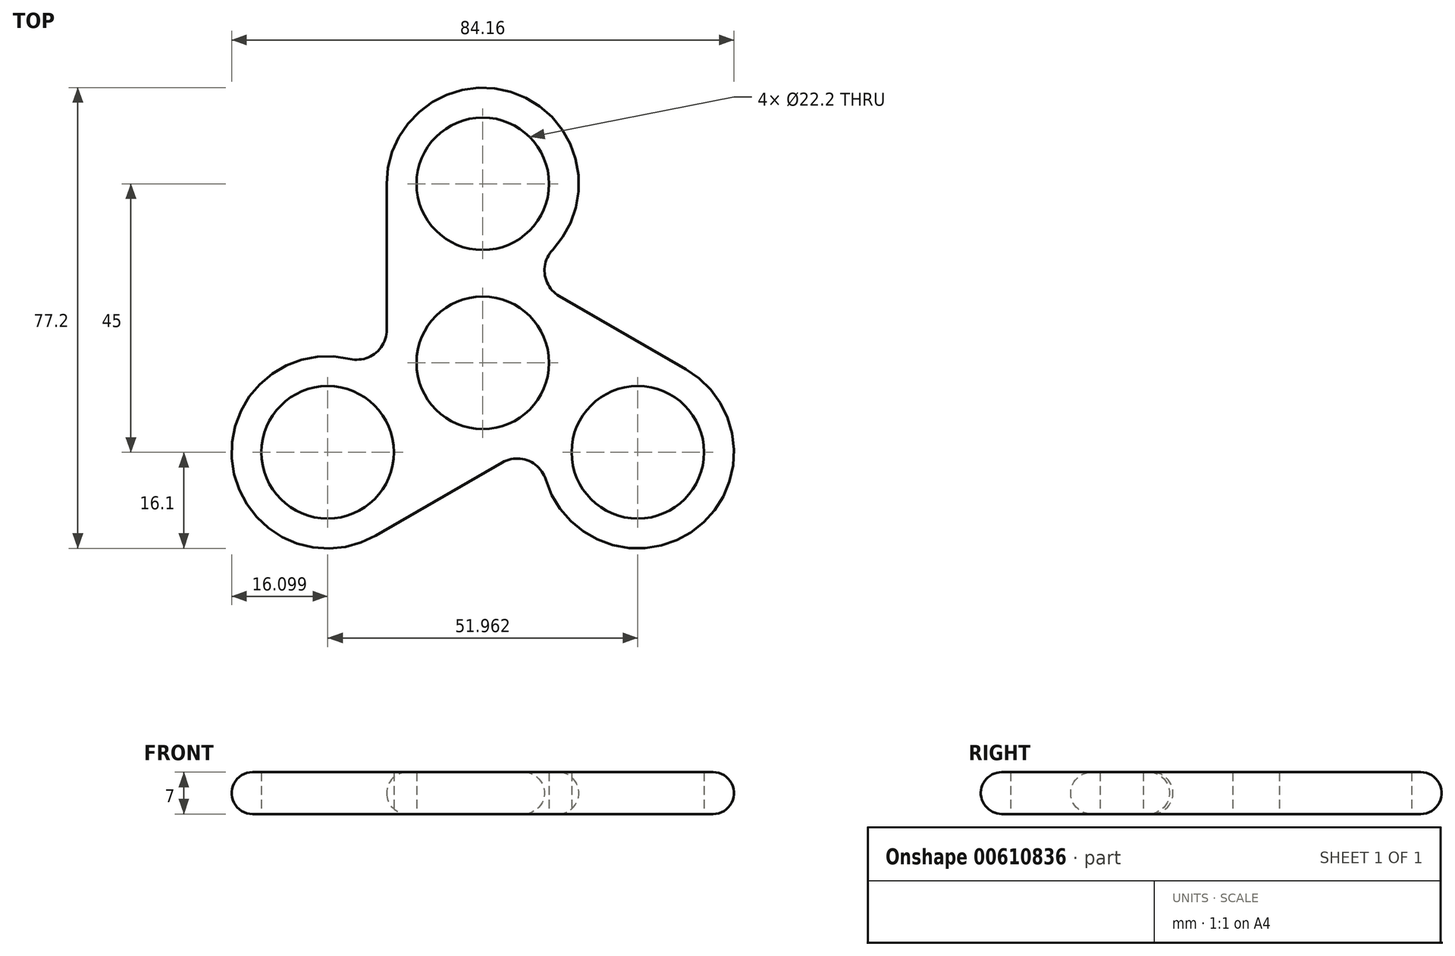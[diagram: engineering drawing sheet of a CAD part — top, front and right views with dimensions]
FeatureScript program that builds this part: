
annotation { "Feature Type Name" : "Feature", "Feature Type Description" : "" }
export const myFeature = defineFeature(function(context is Context, id is Id, definition is map)
    precondition{}
    {
        {
            var Q0;
            Q0=qCreatedBy(makeId("Top.planeOp"),FACE);
            var sketch = newSketch(context, id + "F0", { "sketchPlane" : qUnion([Q0])});
            skCircle(sketch, "E0", {"center": v(0, 0) * mm, "radius": 11.1 * mm});
            skCircle(sketch, "E1", {"center": v(0, 30) * mm, "radius": 11.1 * mm});
            skCircle(sketch, "E2.1.0", {"center": v(-25.98, -15) * mm, "radius": 11.1 * mm});
            skCircle(sketch, "E2.2.0", {"center": v(25.98, -15) * mm, "radius": 11.1 * mm});
            skArc(sketch, "E3.0", {"start": v(6.07, 15.09) * mm, "mid": v(8.99, 43.36) * mm, "end": v(-16.1, 30) * mm});
            skArc(sketch, "E4.1.0", {"start": v(-16.1, -2.29) * mm, "mid": v(-42.04, -13.9) * mm, "end": v(-17.93, -28.94) * mm});
            skArc(sketch, "E4.2.0", {"start": v(10.03, -12.8) * mm, "mid": v(33.06, -29.46) * mm, "end": v(34.03, -1.06) * mm});
            skLineSegment(sketch, "E5", {"start": v(-16.1, 30) * mm, "end": v(-16.1, -2.29) * mm});
            skLineSegment(sketch, "E6.1.0", {"start": v(-17.93, -28.94) * mm, "end": v(10.03, -12.8) * mm});
            skLineSegment(sketch, "E6.2.0", {"start": v(34.03, -1.06) * mm, "end": v(6.07, 15.09) * mm});
            skSolve(sketch);
        }
        {
            var Q0;
            Q0=makeQuery(id+"F0.imprint","IMPRINT",FACE,{"disambiguationData":[TD([[makeQuery(id+"F0.imprint","IMPRINT",EDGE,{"derivedFrom":sQuery(id+"F0.wireOp",EDGE,"E0")}),-1.0]])]});
            extrude(context, id + "F1", {"entities" : qUnion([Q0]), "depth" : 7 * mm, "offsetDistance" : 25 * mm});
        }
        {
            var Q0;
            Q0=makeQuery(id+"F1.opExtrude","SWEPT_EDGE",EDGE,{"disambiguationData":[OSD([sQuery(id+"F0.wireOp",EDGE,"E3.0"),sQuery(id+"F0.wireOp",EDGE,"E6.2.0")])]});
            var Q1;
            Q1=makeQuery(id+"F1.opExtrude","SWEPT_EDGE",EDGE,{"disambiguationData":[OSD([sQuery(id+"F0.wireOp",EDGE,"E4.1.0"),sQuery(id+"F0.wireOp",EDGE,"E5")])]});
            var Q2;
            Q2=makeQuery(id+"F1.opExtrude","SWEPT_EDGE",EDGE,{"disambiguationData":[OSD([sQuery(id+"F0.wireOp",EDGE,"E4.2.0"),sQuery(id+"F0.wireOp",EDGE,"E6.1.0")])]});
            fillet(context, id + "F2", {"entities" : qUnion([Q0, Q1, Q2]), "radius" : 5 * mm, "tangentPropagation" : true, "allowEdgeOverflow" : false});
        }
        {
            var Q0;
            Q0=makeQuery(id+"F1.opExtrude","CAP_EDGE",EDGE,{"disambiguationData":[OSD([sQuery(id+"F0.wireOp",EDGE,"E4.2.0")])],"isStart":false});
            fillet(context, id + "F3", {"entities" : qUnion([Q0]), "radius" : 3.5 * mm, "tangentPropagation" : true, "allowEdgeOverflow" : false});
        }
        {
            var Q0;
            Q0=makeQuery(id+"F1.opExtrude","CAP_EDGE",EDGE,{"disambiguationData":[OSD([sQuery(id+"F0.wireOp",EDGE,"E5")])],"isStart":true});
            fillet(context, id + "F4", {"entities" : qUnion([Q0]), "radius" : 3.5 * mm, "tangentPropagation" : true, "allowEdgeOverflow" : false});
        }
    });
